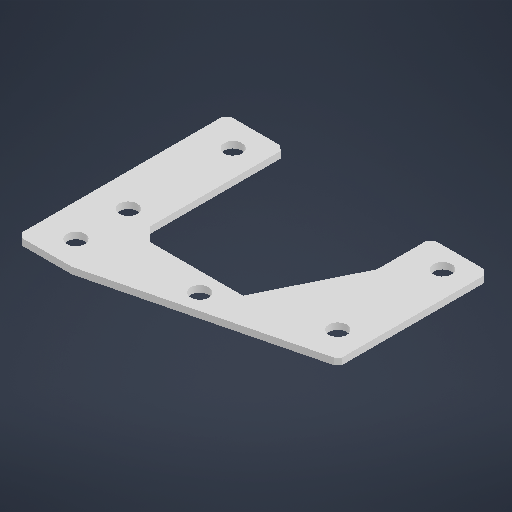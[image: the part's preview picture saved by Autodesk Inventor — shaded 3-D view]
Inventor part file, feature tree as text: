
AUTODESK INVENTOR PART (.ipt)
format: ipt  version: 2025.2 (Build 292293000, 293)  size: 204,800 bytes
history: native  units: in
note: dims shown in document units (in); Inventor stores cm internally (conversion verified against a paired STEP export)
features: extrude x1, sketch x1
ambient origin geometry x8: Origin, YZ Plane, XZ Plane, XY Plane, X Axis, Y Axis, Z Axis, Center Point
bodies: Solid1 (feature_tree)
feature tree (2):
  extrude  "Extrusion1"  Depth=0.0625in
  sketch  "Sketch1"  dims[d0=1.25in d1=0.0625in d2=0.0in d6=0.172in]
